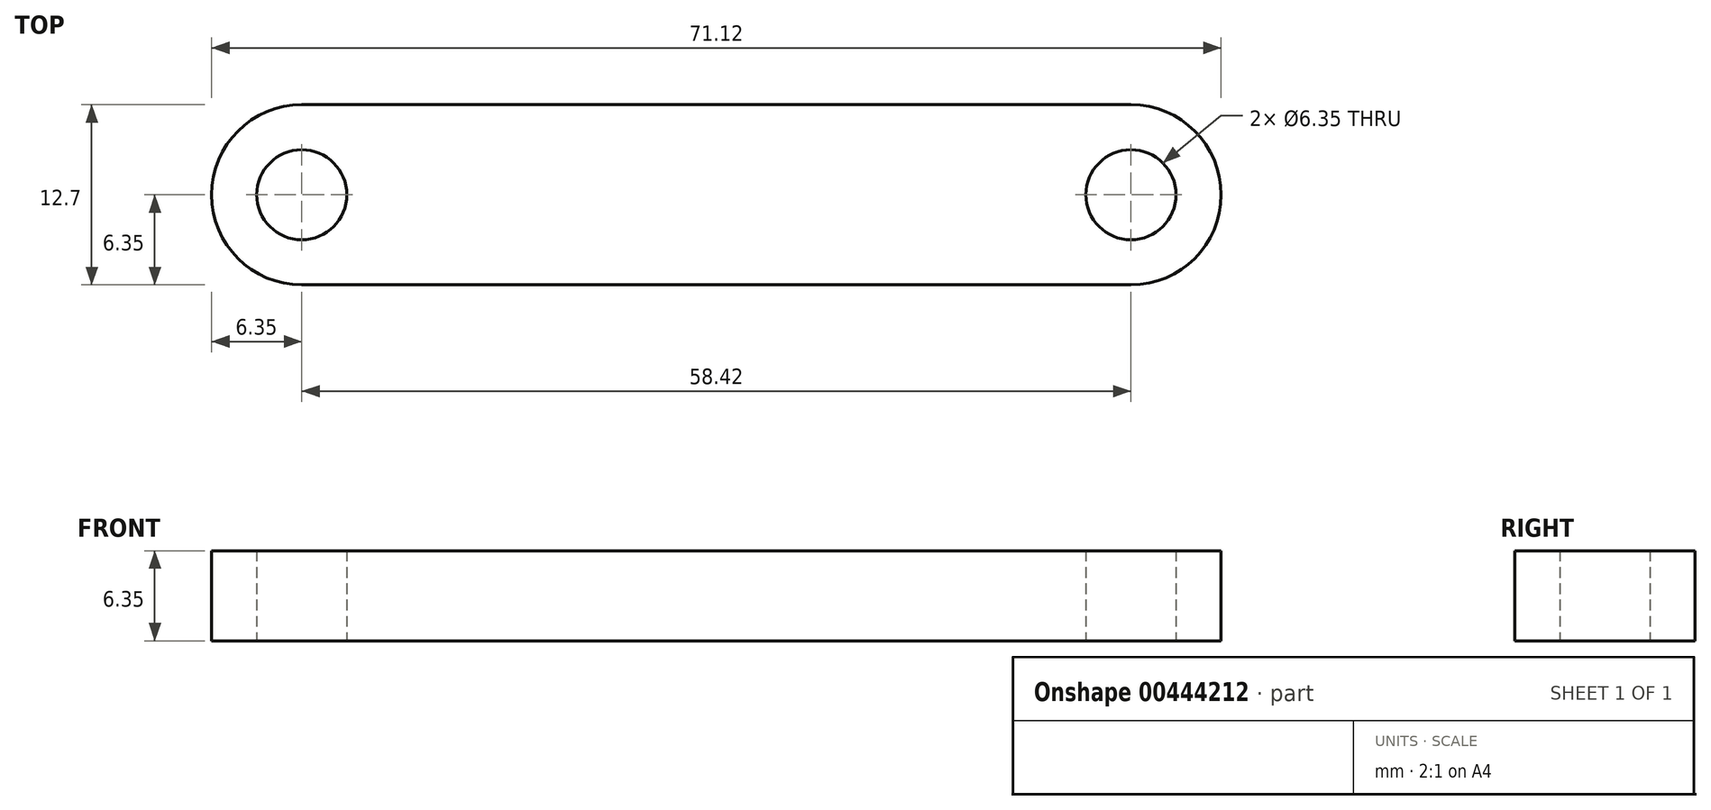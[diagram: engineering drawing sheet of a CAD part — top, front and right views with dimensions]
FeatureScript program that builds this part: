
annotation { "Feature Type Name" : "Feature", "Feature Type Description" : "" }
export const myFeature = defineFeature(function(context is Context, id is Id, definition is map)
    precondition{}
    {
        {
            var Q0;
            Q0=qCreatedBy(makeId("Top.planeOp"),FACE);
            var sketch = newSketch(context, id + "F0", { "sketchPlane" : qUnion([Q0])});
            skCircle(sketch, "E0", {"center": v(0, 0) * mm, "radius": 6.35 * mm});
            skCircle(sketch, "E1", {"center": v(58.42, 0) * mm, "radius": 6.35 * mm});
            skCircle(sketch, "E2", {"center": v(0, 0) * mm, "radius": 3.18 * mm});
            skCircle(sketch, "E3", {"center": v(58.42, 0) * mm, "radius": 3.18 * mm});
            skLineSegment(sketch, "E4", {"start": v(0, 6.35) * mm, "end": v(58.42, 6.35) * mm});
            skLineSegment(sketch, "E5", {"start": v(0, -6.35) * mm, "end": v(58.42, -6.35) * mm});
            skSolve(sketch);
        }
        {
            var Q0;
            Q0 = qSketchRegion(id + "F0", true);
            extrude(context, id + "F1", {"entities" : qUnion([Q0]), "depth" : 6.35 * mm});
        }
    });
